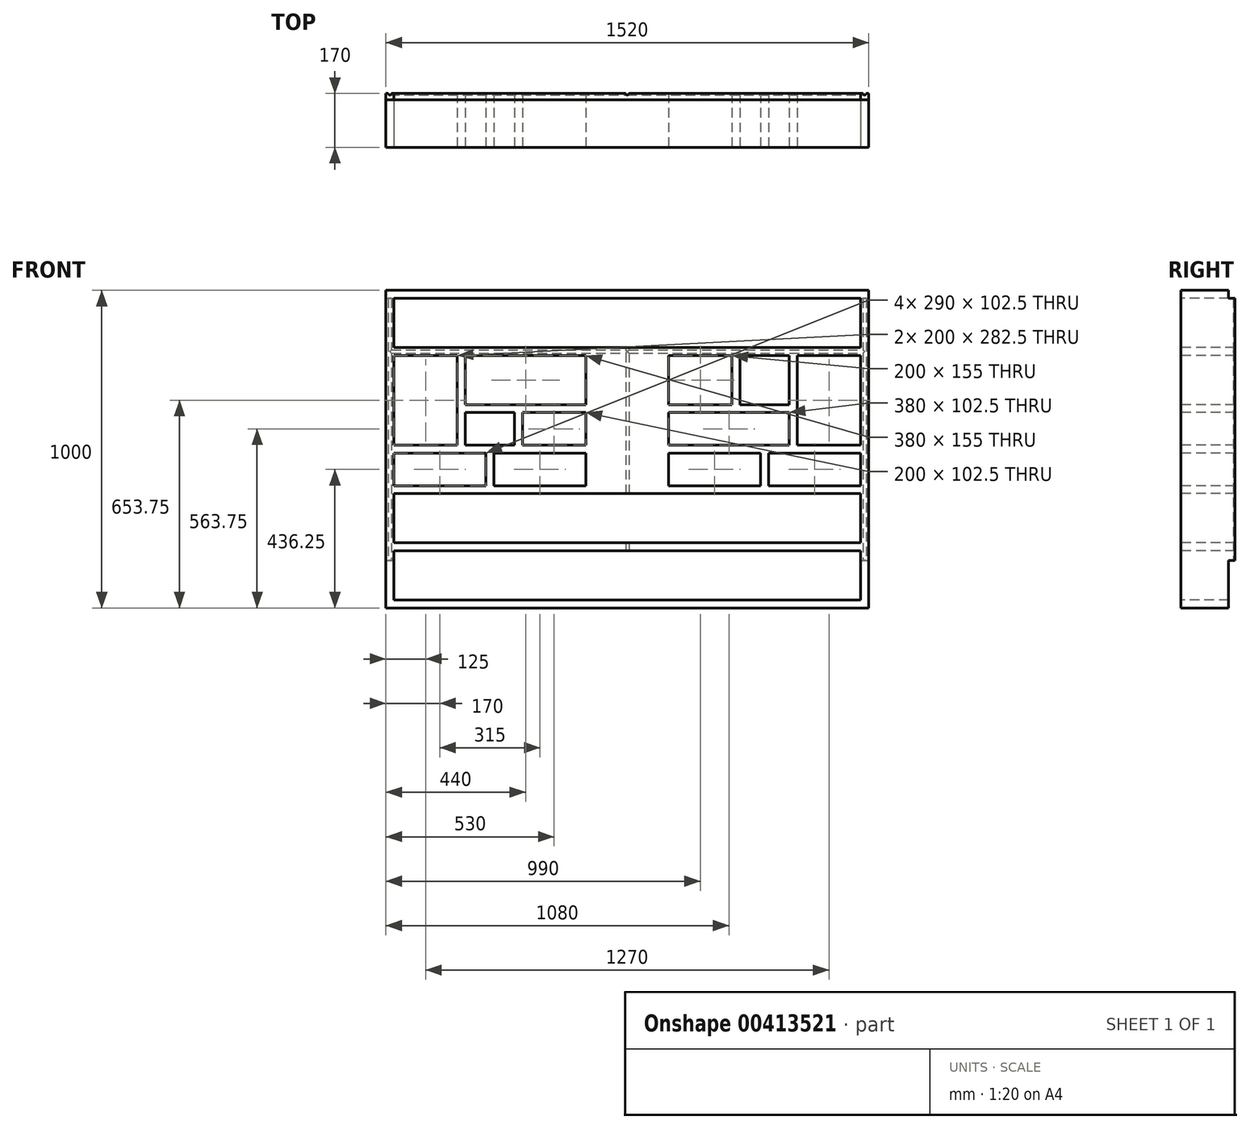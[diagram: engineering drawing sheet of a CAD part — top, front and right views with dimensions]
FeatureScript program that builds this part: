
annotation { "Feature Type Name" : "Feature", "Feature Type Description" : "" }
export const myFeature = defineFeature(function(context is Context, id is Id, definition is map)
    precondition{}
    {
        {
            var Q0;
            Q0=qCreatedBy(makeId("Front.planeOp"),FACE);
            var sketch = newSketch(context, id + "F0", { "sketchPlane" : qUnion([Q0])});
            skLineSegment(sketch, "E0.bottom", {"start": v(760, 500) * mm, "end": v(-760, 500) * mm});
            skLineSegment(sketch, "E0.top", {"start": v(760, -500) * mm, "end": v(-760, -500) * mm});
            skLineSegment(sketch, "E0.left", {"start": v(760, 500) * mm, "end": v(760, -500) * mm});
            skLineSegment(sketch, "E0.right", {"start": v(-760, 500) * mm, "end": v(-760, -500) * mm});
            skPoint(sketch, "E0.middle", {"position": v(0, 0) * mm});
            skSolve(sketch);
        }
        {
            var Q0;
            Q0=makeQuery(id+"F0.imprint","IMPRINT",FACE,{"disambiguationData":[TD([[makeQuery(id+"F0.imprint","IMPRINT",EDGE,{"derivedFrom":sQuery(id+"F0.wireOp",EDGE,"E0.bottom")}),1.0]])]});
            extrude(context, id + "F1", {"entities" : qUnion([Q0]), "oppositeDirection" : true, "offsetDistance" : 25 * mm, "depth" : 170 * mm});
        }
        {
            var Q0;
            Q0=makeQuery(id+"F1.opExtrude","CAP_FACE",FACE,{"disambiguationData":[OSD([sQuery(id+"F0.wireOp",EDGE,"E0.bottom"),sQuery(id+"F0.wireOp",EDGE,"E0.top"),sQuery(id+"F0.wireOp",EDGE,"E0.left"),sQuery(id+"F0.wireOp",EDGE,"E0.right")])],"isStart":true});
            var sketch = newSketch(context, id + "F2", { "sketchPlane" : qUnion([Q0])});
            skLineSegment(sketch, "E1.bottom", {"start": v(-735, -475) * mm, "end": v(735, -475) * mm});
            skLineSegment(sketch, "E1.left", {"start": v(-735, -475) * mm, "end": v(-735, -320) * mm});
            skLineSegment(sketch, "E1.right", {"start": v(735, -475) * mm, "end": v(735, -425) * mm});
            skPoint(sketch, "E2.middle", {"position": v(0, 0) * mm});
            skLineSegment(sketch, "E3", {"start": v(-735, -295) * mm, "end": v(-735, -140) * mm});
            skLineSegment(sketch, "E4", {"start": v(-735, 475) * mm, "end": v(735, 475) * mm});
            skLineSegment(sketch, "E5", {"start": v(735, 475) * mm, "end": v(735, 320) * mm});
            skLineSegment(sketch, "E6", {"start": v(-735, 0) * mm, "end": v(735, 0) * mm, "construction": true});
            skLineSegment(sketch, "E7", {"start": v(-735, -320) * mm, "end": v(735, -320) * mm});
            skLineSegment(sketch, "E8", {"start": v(-735, -295) * mm, "end": v(735, -295) * mm});
            skLineSegment(sketch, "E9", {"start": v(-735, -140) * mm, "end": v(735, -140) * mm});
            skLineSegment(sketch, "E10", {"start": v(-735, -115) * mm, "end": v(735, -115) * mm});
            skLineSegment(sketch, "E11", {"start": v(-735, -12.5) * mm, "end": v(-105, -12.5) * mm});
            skLineSegment(sketch, "E12", {"start": v(-735, 12.5) * mm, "end": v(-105, 12.5) * mm});
            skLineSegment(sketch, "E13.MirrorCS", {"start": v(-735, 320) * mm, "end": v(735, 320) * mm});
            skLineSegment(sketch, "E14.MirrorCS", {"start": v(-735, 295) * mm, "end": v(735, 295) * mm});
            skLineSegment(sketch, "E15.MirrorCS", {"start": v(-535, 115) * mm, "end": v(-105, 115) * mm});
            skLineSegment(sketch, "E16.MirrorCS", {"start": v(-535, 140) * mm, "end": v(-105, 140) * mm});
            skLineSegment(sketch, "E17.trimOffspring", {"start": v(735, 295) * mm, "end": v(735, 140) * mm});
            skLineSegment(sketch, "E18.trimOffspring", {"start": v(-735, 320) * mm, "end": v(-735, 475) * mm});
            skLineSegment(sketch, "E19.trimOffspring", {"start": v(-735, 140) * mm, "end": v(-735, 295) * mm});
            skLineSegment(sketch, "E20.trimOffspring", {"start": v(-735, 12.5) * mm, "end": v(-735, 115) * mm});
            skLineSegment(sketch, "E21.trimOffspring", {"start": v(-735, -115) * mm, "end": v(-735, -12.5) * mm});
            skLineSegment(sketch, "E22.trimOffspring", {"start": v(735, -320) * mm, "end": v(735, -425) * mm});
            skLineSegment(sketch, "E23.trimOffspring", {"start": v(735, -140) * mm, "end": v(735, -295) * mm});
            skLineSegment(sketch, "E24.trimOffspring", {"start": v(735, 115) * mm, "end": v(735, 12.5) * mm});
            skLineSegment(sketch, "E25.trimOffspring", {"start": v(735, -12.5) * mm, "end": v(735, -115) * mm});
            skLineSegment(sketch, "E26", {"start": v(0, 0) * mm, "end": v(0, 295) * mm, "construction": true});
            skLineSegment(sketch, "E27", {"start": v(535, 295) * mm, "end": v(535, 12.5) * mm});
            skLineSegment(sketch, "E28", {"start": v(510, 295) * mm, "end": v(510, 12.5) * mm});
            skLineSegment(sketch, "E29", {"start": v(330, 295) * mm, "end": v(330, 140) * mm});
            skLineSegment(sketch, "E30", {"start": v(355, 295) * mm, "end": v(355, 140) * mm});
            skLineSegment(sketch, "E31.MirrorCS", {"start": v(-510, 295) * mm, "end": v(-510, 12.5) * mm});
            skLineSegment(sketch, "E32.MirrorCS", {"start": v(-535, 295) * mm, "end": v(-535, 12.5) * mm});
            skLineSegment(sketch, "E33", {"start": v(-330, 12.5) * mm, "end": v(-330, 140) * mm});
            skLineSegment(sketch, "E34", {"start": v(-355, 140) * mm, "end": v(-355, 12.5) * mm});
            skPoint(sketch, "E35.MirrorCS.start.orphan", {"position": v(-330, 295) * mm});
            skPoint(sketch, "E36.MirrorCS.start.orphan", {"position": v(-355, 295) * mm});
            skLineSegment(sketch, "E37", {"start": v(-735, 140) * mm, "end": v(-735, 115) * mm});
            skLineSegment(sketch, "E38", {"start": v(735, 115) * mm, "end": v(735, 140) * mm});
            skLineSegment(sketch, "E39", {"start": v(105, 295) * mm, "end": v(105, 12.5) * mm});
            skLineSegment(sketch, "E40", {"start": v(130, 295) * mm, "end": v(130, 12.5) * mm});
            skLineSegment(sketch, "E41.MirrorCS", {"start": v(-130, 295) * mm, "end": v(-130, 12.5) * mm});
            skLineSegment(sketch, "E42.MirrorCS", {"start": v(-105, 295) * mm, "end": v(-105, 12.5) * mm});
            skLineSegment(sketch, "E43.trimOffspring", {"start": v(105, 115) * mm, "end": v(535, 115) * mm});
            skLineSegment(sketch, "E44.trimOffspring", {"start": v(105, 140) * mm, "end": v(535, 140) * mm});
            skLineSegment(sketch, "E45", {"start": v(105, -12.5) * mm, "end": v(105, -115) * mm});
            skLineSegment(sketch, "E46", {"start": v(130, -12.5) * mm, "end": v(130, -115) * mm});
            skLineSegment(sketch, "E47", {"start": v(-130, -12.5) * mm, "end": v(-130, -115) * mm});
            skLineSegment(sketch, "E48", {"start": v(-105, -12.5) * mm, "end": v(-105, -115) * mm});
            skLineSegment(sketch, "E49", {"start": v(-105, 12.5) * mm, "end": v(-105, -12.5) * mm});
            skLineSegment(sketch, "E50", {"start": v(105, 12.5) * mm, "end": v(105, -12.5) * mm});
            skLineSegment(sketch, "E51", {"start": v(130, 12.5) * mm, "end": v(735, 12.5) * mm});
            skLineSegment(sketch, "E52", {"start": v(735, -12.5) * mm, "end": v(130, -12.5) * mm});
            skLineSegment(sketch, "E53", {"start": v(445, -12.5) * mm, "end": v(445, -115) * mm});
            skLineSegment(sketch, "E54", {"start": v(420, -12.5) * mm, "end": v(420, -115) * mm});
            skLineSegment(sketch, "E55", {"start": v(-445, -12.5) * mm, "end": v(-445, -115) * mm});
            skLineSegment(sketch, "E56", {"start": v(-420, -12.5) * mm, "end": v(-420, -115) * mm});
            skSolve(sketch);
        }
        {
            var Q0;
            Q0=makeQuery(id+"F2.imprint","IMPRINT",FACE,{"disambiguationData":[TD([[makeQuery(id+"F2.imprint","IMPRINT",EDGE,{"derivedFrom":sQuery(id+"F2.wireOp",EDGE,"E4")}),-1.0]])]});
            var Q1;
            Q1=makeQuery(id+"F2.imprint","IMPRINT",FACE,{"disambiguationData":[TD([[makeQuery(id+"F2.imprint","IMPRINT",EDGE,{"derivedFrom":sQuery(id+"F2.wireOp",EDGE,"E14.MirrorCS")}),-1.0]])]});
            var Q2;
            Q2=makeQuery(id+"F2.imprint","IMPRINT",FACE,{"disambiguationData":[TD([[makeQuery(id+"F2.imprint","IMPRINT",EDGE,{"derivedFrom":sQuery(id+"F2.wireOp",EDGE,"E12")}),1.0]])]});
            var Q3;
            Q3=makeQuery(id+"F2.imprint","IMPRINT",FACE,{"disambiguationData":[TD([[makeQuery(id+"F2.imprint","IMPRINT",EDGE,{"derivedFrom":sQuery(id+"F2.wireOp",EDGE,"E10")}),1.0]])]});
            var Q4;
            Q4=makeQuery(id+"F2.imprint","IMPRINT",FACE,{"disambiguationData":[TD([[makeQuery(id+"F2.imprint","IMPRINT",EDGE,{"derivedFrom":sQuery(id+"F2.wireOp",EDGE,"E3")}),-1.0]])]});
            var Q5;
            Q5=makeQuery(id+"F2.imprint","IMPRINT",FACE,{"disambiguationData":[TD([[makeQuery(id+"F2.imprint","IMPRINT",EDGE,{"derivedFrom":sQuery(id+"F2.wireOp",EDGE,"E1.bottom")}),1.0]])]});
            var Q6;
            Q6=makeQuery(id+"F1.opExtrude","CAP_FACE",FACE,{"disambiguationData":[OSD([sQuery(id+"F0.wireOp",EDGE,"E0.bottom"),sQuery(id+"F0.wireOp",EDGE,"E0.top"),sQuery(id+"F0.wireOp",EDGE,"E0.left"),sQuery(id+"F0.wireOp",EDGE,"E0.right")])],"isStart":false});
            extrude(context, id + "F3", {"entities" : qUnion([Q0, Q1, Q2, Q3, Q4, Q5]), "operationType" : NewBodyOperationType.REMOVE, "endBound" : BoundingType.UP_TO_SURFACE, "oppositeDirection" : true, "depth" : 25 * mm, "endBoundEntityFace" : qUnion([Q6]), "offsetDistance" : 25 * mm});
        }
        {
            var Q0;
            {var subQ0=sQuery(id+"F2.wireOp",EDGE,"E31.MirrorCS");var subQ1=sQuery(id+"F2.wireOp",EDGE,"E14.MirrorCS");var subQ2=makeQuery(id+"F2.imprint","INTERSECT",VERTEX,{"derivedFrom":[subQ1,subQ0]});Q0=makeQuery(id+"F2.imprint","IMPRINT",FACE,{"disambiguationData":[TD([[makeQuery(id+"F2.imprint","IMPRINT",EDGE,{"disambiguationData":[TD([[subQ2,1.0]])],"derivedFrom":subQ1}),-1.0]])]});}
            var Q1;
            {var subQ0=sQuery(id+"F2.wireOp",EDGE,"E32.MirrorCS");var subQ1=sQuery(id+"F2.wireOp",EDGE,"E15.MirrorCS");var subQ2=makeQuery(id+"F2.imprint","INTERSECT",VERTEX,{"derivedFrom":[subQ1,subQ0]});Q1=makeQuery(id+"F2.imprint","IMPRINT",FACE,{"disambiguationData":[TD([[makeQuery(id+"F2.imprint","IMPRINT",EDGE,{"disambiguationData":[TD([[subQ2,-1.0]])],"derivedFrom":subQ1}),1.0]])]});}
            var Q2;
            {var subQ0=sQuery(id+"F2.wireOp",EDGE,"E31.MirrorCS");var subQ1=sQuery(id+"F2.wireOp",EDGE,"E12");var subQ2=makeQuery(id+"F2.imprint","INTERSECT",VERTEX,{"derivedFrom":[subQ1,subQ0]});Q2=makeQuery(id+"F2.imprint","IMPRINT",FACE,{"disambiguationData":[TD([[makeQuery(id+"F2.imprint","IMPRINT",EDGE,{"disambiguationData":[TD([[subQ2,1.0]])],"derivedFrom":subQ1}),1.0]])]});}
            var Q3;
            {var subQ0=sQuery(id+"F2.wireOp",EDGE,"E31.MirrorCS");var subQ1=sQuery(id+"F2.wireOp",EDGE,"E15.MirrorCS");var subQ2=makeQuery(id+"F2.imprint","INTERSECT",VERTEX,{"derivedFrom":[subQ1,subQ0]});Q3=makeQuery(id+"F2.imprint","IMPRINT",FACE,{"disambiguationData":[TD([[makeQuery(id+"F2.imprint","IMPRINT",EDGE,{"disambiguationData":[TD([[subQ2,-1.0]])],"derivedFrom":subQ1}),1.0]])]});}
            var Q4;
            {var subQ0=sQuery(id+"F2.wireOp",EDGE,"E34");var subQ1=sQuery(id+"F2.wireOp",EDGE,"E15.MirrorCS");var subQ2=makeQuery(id+"F2.imprint","INTERSECT",VERTEX,{"derivedFrom":[subQ1,subQ0]});Q4=makeQuery(id+"F2.imprint","IMPRINT",FACE,{"disambiguationData":[TD([[makeQuery(id+"F2.imprint","IMPRINT",EDGE,{"disambiguationData":[TD([[subQ2,-1.0]])],"derivedFrom":subQ1}),1.0]])]});}
            var Q5;
            {var subQ0=sQuery(id+"F2.wireOp",EDGE,"E33");var subQ1=sQuery(id+"F2.wireOp",EDGE,"E12");var subQ2=makeQuery(id+"F2.imprint","INTERSECT",VERTEX,{"derivedFrom":[subQ1,subQ0]});Q5=makeQuery(id+"F2.imprint","IMPRINT",FACE,{"disambiguationData":[TD([[makeQuery(id+"F2.imprint","IMPRINT",EDGE,{"disambiguationData":[TD([[subQ2,1.0]])],"derivedFrom":subQ1}),1.0]])]});}
            var Q6;
            {var subQ0=sQuery(id+"F2.wireOp",EDGE,"E33");var subQ1=sQuery(id+"F2.wireOp",EDGE,"E15.MirrorCS");var subQ2=makeQuery(id+"F2.imprint","INTERSECT",VERTEX,{"derivedFrom":[subQ1,subQ0]});Q6=makeQuery(id+"F2.imprint","IMPRINT",FACE,{"disambiguationData":[TD([[makeQuery(id+"F2.imprint","IMPRINT",EDGE,{"disambiguationData":[TD([[subQ2,-1.0]])],"derivedFrom":subQ1}),1.0]])]});}
            var Q7;
            {var subQ0=sQuery(id+"F2.wireOp",EDGE,"eI3SPyVD-0uEl-pIWH-4MRa-sc1sVIOGqZNf");var subQ1=sQuery(id+"F2.wireOp",EDGE,"E12");var subQ2=makeQuery(id+"F2.imprint","INTERSECT",VERTEX,{"derivedFrom":[subQ1,subQ0]});Q7=makeQuery(id+"F2.imprint","IMPRINT",FACE,{"disambiguationData":[TD([[makeQuery(id+"F2.imprint","IMPRINT",EDGE,{"disambiguationData":[TD([[subQ2,1.0]])],"derivedFrom":subQ1}),1.0]])]});}
            var Q8;
            {var subQ0=sQuery(id+"F2.wireOp",EDGE,"ZKDIpnAd-JpXH-PnlA-Ugrf-fCPR0U1nQhHu");var subQ1=sQuery(id+"F2.wireOp",EDGE,"E15.MirrorCS");var subQ2=makeQuery(id+"F2.imprint","INTERSECT",VERTEX,{"derivedFrom":[subQ1,subQ0]});Q8=makeQuery(id+"F2.imprint","IMPRINT",FACE,{"disambiguationData":[TD([[makeQuery(id+"F2.imprint","IMPRINT",EDGE,{"disambiguationData":[TD([[subQ2,-1.0]])],"derivedFrom":subQ1}),1.0]])]});}
            var Q9;
            {var subQ0=sQuery(id+"F2.wireOp",EDGE,"eI3SPyVD-0uEl-pIWH-4MRa-sc1sVIOGqZNf");var subQ1=sQuery(id+"F2.wireOp",EDGE,"E14.MirrorCS");var subQ2=makeQuery(id+"F2.imprint","INTERSECT",VERTEX,{"derivedFrom":[subQ1,subQ0]});Q9=makeQuery(id+"F2.imprint","IMPRINT",FACE,{"disambiguationData":[TD([[makeQuery(id+"F2.imprint","IMPRINT",EDGE,{"disambiguationData":[TD([[subQ2,1.0]])],"derivedFrom":subQ1}),-1.0]])]});}
            var Q10;
            {var subQ0=sQuery(id+"F2.wireOp",EDGE,"E29");Q10=makeQuery(id+"F2.imprint","IMPRINT",FACE,{"disambiguationData":[TD([[makeQuery(id+"F2.imprint","IMPRINT",EDGE,{"derivedFrom":subQ0}),1.0]])]});}
            var Q11;
            {var subQ5=sQuery(id+"F2.wireOp",EDGE,"eI3SPyVD-0uEl-pIWH-4MRa-sc1sVIOGqZNf");var subQ6=sQuery(id+"F2.wireOp",EDGE,"E15.MirrorCS");var subQ7=makeQuery(id+"F2.imprint","INTERSECT",VERTEX,{"derivedFrom":[subQ6,subQ5]});Q11=makeQuery(id+"F2.imprint","IMPRINT",FACE,{"disambiguationData":[TD([[makeQuery(id+"F2.imprint","IMPRINT",EDGE,{"disambiguationData":[TD([[subQ7,-1.0]])],"derivedFrom":subQ6}),1.0]])]});}
            var Q12;
            {var subQ0=sQuery(id+"F2.wireOp",EDGE,"E27");var subQ1=sQuery(id+"F2.wireOp",EDGE,"E12");var subQ2=makeQuery(id+"F2.imprint","INTERSECT",VERTEX,{"derivedFrom":[subQ1,subQ0]});Q12=makeQuery(id+"F2.imprint","IMPRINT",FACE,{"disambiguationData":[TD([[makeQuery(id+"F2.imprint","IMPRINT",EDGE,{"disambiguationData":[TD([[subQ2,1.0]])],"derivedFrom":subQ1}),1.0]])]});}
            var Q13;
            {var subQ0=sQuery(id+"F2.wireOp",EDGE,"E27");var subQ1=sQuery(id+"F2.wireOp",EDGE,"E15.MirrorCS");var subQ2=makeQuery(id+"F2.imprint","INTERSECT",VERTEX,{"derivedFrom":[subQ1,subQ0]});Q13=makeQuery(id+"F2.imprint","IMPRINT",FACE,{"disambiguationData":[TD([[makeQuery(id+"F2.imprint","IMPRINT",EDGE,{"disambiguationData":[TD([[subQ2,1.0]])],"derivedFrom":subQ1}),1.0]])]});}
            var Q14;
            {var subQ0=sQuery(id+"F2.wireOp",EDGE,"E27");var subQ1=sQuery(id+"F2.wireOp",EDGE,"E14.MirrorCS");var subQ2=makeQuery(id+"F2.imprint","INTERSECT",VERTEX,{"derivedFrom":[subQ1,subQ0]});Q14=makeQuery(id+"F2.imprint","IMPRINT",FACE,{"disambiguationData":[TD([[makeQuery(id+"F2.imprint","IMPRINT",EDGE,{"disambiguationData":[TD([[subQ2,1.0]])],"derivedFrom":subQ1}),-1.0]])]});}
            var Q15;
            Q15=makeQuery(id+"F1.opExtrude","CAP_FACE",FACE,{"disambiguationData":[OSD([sQuery(id+"F0.wireOp",EDGE,"E0.bottom"),sQuery(id+"F0.wireOp",EDGE,"E0.top"),sQuery(id+"F0.wireOp",EDGE,"E0.left"),sQuery(id+"F0.wireOp",EDGE,"E0.right")])],"isStart":false});
            extrude(context, id + "F4", {"entities" : qUnion([Q0, Q1, Q2, Q3, Q4, Q5, Q6, Q7, Q8, Q9, Q10, Q11, Q12, Q13, Q14]), "operationType" : NewBodyOperationType.ADD, "endBound" : BoundingType.UP_TO_SURFACE, "oppositeDirection" : true, "depth" : 25 * mm, "endBoundEntityFace" : qUnion([Q15]), "offsetDistance" : 25 * mm});
        }
        {
            var Q0;
            {var subQ1=sQuery(id+"F2.wireOp",EDGE,"E19.trimOffspring");Q0=makeQuery(id+"F2.imprint","IMPRINT",FACE,{"disambiguationData":[TD([[makeQuery(id+"F2.imprint","IMPRINT",EDGE,{"derivedFrom":subQ1}),-1.0]])]});}
            var Q1;
            {var subQ2=sQuery(id+"F2.wireOp",EDGE,"ZKDIpnAd-JpXH-PnlA-Ugrf-fCPR0U1nQhHu");var subQ7=sQuery(id+"F2.wireOp",EDGE,"E14.MirrorCS");var subQ8=makeQuery(id+"F2.imprint","INTERSECT",VERTEX,{"derivedFrom":[subQ7,subQ2]});Q1=makeQuery(id+"F2.imprint","IMPRINT",FACE,{"disambiguationData":[TD([[makeQuery(id+"F2.imprint","IMPRINT",EDGE,{"disambiguationData":[TD([[subQ8,1.0]])],"derivedFrom":subQ7}),-1.0]])]});}
            var Q2;
            {var subQ1=sQuery(id+"F2.wireOp",EDGE,"E17.trimOffspring");Q2=makeQuery(id+"F2.imprint","IMPRINT",FACE,{"disambiguationData":[TD([[makeQuery(id+"F2.imprint","IMPRINT",EDGE,{"derivedFrom":subQ1}),-1.0]])]});}
            var Q3;
            Q3=makeQuery(id+"F4.boolean.opBoolean","MERGE",FACE,{"derivedFrom":[makeQuery(id+"F1.opExtrude","CAP_FACE",FACE,{"disambiguationData":[OSD([sQuery(id+"F0.wireOp",EDGE,"E0.bottom"),sQuery(id+"F0.wireOp",EDGE,"E0.top"),sQuery(id+"F0.wireOp",EDGE,"E0.left"),sQuery(id+"F0.wireOp",EDGE,"E0.right")])],"isStart":false}),makeQuery(id+"F4.opExtrude","CAP_FACE",FACE,{"disambiguationData":[OSD([sQuery(id+"F2.wireOp",EDGE,"E12"),sQuery(id+"F2.wireOp",EDGE,"E14.MirrorCS"),sQuery(id+"F2.wireOp",EDGE,"E15.MirrorCS"),sQuery(id+"F2.wireOp",EDGE,"E16.MirrorCS"),sQuery(id+"F2.wireOp",EDGE,"eI3SPyVD-0uEl-pIWH-4MRa-sc1sVIOGqZNf"),sQuery(id+"F2.wireOp",EDGE,"ZKDIpnAd-JpXH-PnlA-Ugrf-fCPR0U1nQhHu"),sQuery(id+"F2.wireOp",EDGE,"E27"),sQuery(id+"F2.wireOp",EDGE,"E28"),sQuery(id+"F2.wireOp",EDGE,"E29"),sQuery(id+"F2.wireOp",EDGE,"E30"),sQuery(id+"F2.wireOp",EDGE,"E31.MirrorCS"),sQuery(id+"F2.wireOp",EDGE,"E32.MirrorCS"),sQuery(id+"F2.wireOp",EDGE,"E33"),sQuery(id+"F2.wireOp",EDGE,"E34")])],"isStart":false})]});
            extrude(context, id + "F5", {"entities" : qUnion([Q0, Q1, Q2]), "operationType" : NewBodyOperationType.REMOVE, "endBound" : BoundingType.UP_TO_SURFACE, "oppositeDirection" : true, "depth" : 25 * mm, "endBoundEntityFace" : qUnion([Q3]), "offsetDistance" : 25 * mm});
        }
        {
            var Q0;
            {var subQ0=sQuery(id+"F2.wireOp",EDGE,"E29");Q0=makeQuery(id+"F2.imprint","IMPRINT",FACE,{"disambiguationData":[TD([[makeQuery(id+"F2.imprint","IMPRINT",EDGE,{"derivedFrom":subQ0}),1.0]])]});}
            var Q1;
            {var subQ0=sQuery(id+"F2.wireOp",EDGE,"E44.trimOffspring");var subQ5=sQuery(id+"F2.wireOp",EDGE,"E28");var subQ8=makeQuery(id+"F2.imprint","INTERSECT",VERTEX,{"derivedFrom":[subQ5,subQ0]});Q1=makeQuery(id+"F2.imprint","IMPRINT",FACE,{"disambiguationData":[TD([[makeQuery(id+"F2.imprint","IMPRINT",EDGE,{"disambiguationData":[TD([[subQ8,-1.0]])],"derivedFrom":subQ5}),-1.0]])]});}
            var Q2;
            {var subQ0=sQuery(id+"F2.wireOp",EDGE,"E27");var subQ1=sQuery(id+"F2.wireOp",EDGE,"E14.MirrorCS");var subQ2=makeQuery(id+"F2.imprint","INTERSECT",VERTEX,{"derivedFrom":[subQ1,subQ0]});Q2=makeQuery(id+"F2.imprint","IMPRINT",FACE,{"disambiguationData":[TD([[makeQuery(id+"F2.imprint","IMPRINT",EDGE,{"disambiguationData":[TD([[subQ2,1.0]])],"derivedFrom":subQ1}),-1.0]])]});}
            var Q3;
            {var subQ0=sQuery(id+"F2.wireOp",EDGE,"E43.trimOffspring");var subQ1=sQuery(id+"F2.wireOp",EDGE,"E27");var subQ2=makeQuery(id+"F2.imprint","INTERSECT",VERTEX,{"derivedFrom":[subQ1,subQ0]});Q3=makeQuery(id+"F2.imprint","IMPRINT",FACE,{"disambiguationData":[TD([[makeQuery(id+"F2.imprint","IMPRINT",EDGE,{"disambiguationData":[TD([[subQ2,1.0]])],"derivedFrom":subQ1}),-1.0]])]});}
            var Q4;
            {var subQ0=sQuery(id+"F2.wireOp",EDGE,"E27");var subQ1=sQuery(id+"F2.wireOp",EDGE,"E12");var subQ2=makeQuery(id+"F2.imprint","INTERSECT",VERTEX,{"derivedFrom":[subQ1,subQ0]});Q4=makeQuery(id+"F2.imprint","IMPRINT",FACE,{"disambiguationData":[TD([[makeQuery(id+"F2.imprint","IMPRINT",EDGE,{"disambiguationData":[TD([[subQ2,1.0]])],"derivedFrom":subQ1}),1.0]])]});}
            var Q5;
            {var subQ0=sQuery(id+"F2.wireOp",EDGE,"E39");var subQ1=sQuery(id+"F2.wireOp",EDGE,"E12");var subQ2=makeQuery(id+"F2.imprint","INTERSECT",VERTEX,{"derivedFrom":[subQ1,subQ0]});Q5=makeQuery(id+"F2.imprint","IMPRINT",FACE,{"disambiguationData":[TD([[makeQuery(id+"F2.imprint","IMPRINT",EDGE,{"disambiguationData":[TD([[subQ2,-1.0]])],"derivedFrom":subQ1}),1.0]])]});}
            var Q6;
            {var subQ0=sQuery(id+"F2.wireOp",EDGE,"E43.trimOffspring");var subQ1=sQuery(id+"F2.wireOp",EDGE,"E39");var subQ2=makeQuery(id+"F2.imprint","INTERSECT",VERTEX,{"derivedFrom":[subQ1,subQ0]});Q6=makeQuery(id+"F2.imprint","IMPRINT",FACE,{"disambiguationData":[TD([[makeQuery(id+"F2.imprint","IMPRINT",EDGE,{"disambiguationData":[TD([[subQ2,1.0]])],"derivedFrom":subQ1}),1.0]])]});}
            var Q7;
            {var subQ0=sQuery(id+"F2.wireOp",EDGE,"E39");var subQ1=sQuery(id+"F2.wireOp",EDGE,"E14.MirrorCS");var subQ2=makeQuery(id+"F2.imprint","INTERSECT",VERTEX,{"derivedFrom":[subQ1,subQ0]});Q7=makeQuery(id+"F2.imprint","IMPRINT",FACE,{"disambiguationData":[TD([[makeQuery(id+"F2.imprint","IMPRINT",EDGE,{"disambiguationData":[TD([[subQ2,-1.0]])],"derivedFrom":subQ1}),-1.0]])]});}
            var Q8;
            {var subQ0=sQuery(id+"F2.wireOp",EDGE,"E41.MirrorCS");var subQ1=sQuery(id+"F2.wireOp",EDGE,"E14.MirrorCS");var subQ2=makeQuery(id+"F2.imprint","INTERSECT",VERTEX,{"derivedFrom":[subQ1,subQ0]});Q8=makeQuery(id+"F2.imprint","IMPRINT",FACE,{"disambiguationData":[TD([[makeQuery(id+"F2.imprint","IMPRINT",EDGE,{"disambiguationData":[TD([[subQ2,-1.0]])],"derivedFrom":subQ1}),-1.0]])]});}
            var Q9;
            {var subQ0=sQuery(id+"F2.wireOp",EDGE,"E42.MirrorCS");var subQ1=sQuery(id+"F2.wireOp",EDGE,"E15.MirrorCS");var subQ2=makeQuery(id+"F2.imprint","INTERSECT",VERTEX,{"derivedFrom":[subQ1,subQ0]});Q9=makeQuery(id+"F2.imprint","IMPRINT",FACE,{"disambiguationData":[TD([[makeQuery(id+"F2.imprint","IMPRINT",EDGE,{"disambiguationData":[TD([[subQ2,1.0]])],"derivedFrom":subQ1}),1.0]])]});}
            var Q10;
            {var subQ0=sQuery(id+"F2.wireOp",EDGE,"E41.MirrorCS");var subQ1=sQuery(id+"F2.wireOp",EDGE,"E12");var subQ2=makeQuery(id+"F2.imprint","INTERSECT",VERTEX,{"derivedFrom":[subQ1,subQ0]});Q10=makeQuery(id+"F2.imprint","IMPRINT",FACE,{"disambiguationData":[TD([[makeQuery(id+"F2.imprint","IMPRINT",EDGE,{"disambiguationData":[TD([[subQ2,-1.0]])],"derivedFrom":subQ1}),1.0]])]});}
            var Q11;
            {var subQ0=sQuery(id+"F2.wireOp",EDGE,"E33");var subQ1=sQuery(id+"F2.wireOp",EDGE,"E15.MirrorCS");var subQ2=makeQuery(id+"F2.imprint","INTERSECT",VERTEX,{"derivedFrom":[subQ1,subQ0]});Q11=makeQuery(id+"F2.imprint","IMPRINT",FACE,{"disambiguationData":[TD([[makeQuery(id+"F2.imprint","IMPRINT",EDGE,{"disambiguationData":[TD([[subQ2,-1.0]])],"derivedFrom":subQ1}),1.0]])]});}
            var Q12;
            {var subQ0=sQuery(id+"F2.wireOp",EDGE,"E33");var subQ1=sQuery(id+"F2.wireOp",EDGE,"E12");var subQ2=makeQuery(id+"F2.imprint","INTERSECT",VERTEX,{"derivedFrom":[subQ1,subQ0]});Q12=makeQuery(id+"F2.imprint","IMPRINT",FACE,{"disambiguationData":[TD([[makeQuery(id+"F2.imprint","IMPRINT",EDGE,{"disambiguationData":[TD([[subQ2,1.0]])],"derivedFrom":subQ1}),1.0]])]});}
            var Q13;
            {var subQ0=sQuery(id+"F2.wireOp",EDGE,"E34");var subQ1=sQuery(id+"F2.wireOp",EDGE,"E15.MirrorCS");var subQ2=makeQuery(id+"F2.imprint","INTERSECT",VERTEX,{"derivedFrom":[subQ1,subQ0]});Q13=makeQuery(id+"F2.imprint","IMPRINT",FACE,{"disambiguationData":[TD([[makeQuery(id+"F2.imprint","IMPRINT",EDGE,{"disambiguationData":[TD([[subQ2,-1.0]])],"derivedFrom":subQ1}),1.0]])]});}
            var Q14;
            {var subQ0=sQuery(id+"F2.wireOp",EDGE,"E31.MirrorCS");var subQ1=sQuery(id+"F2.wireOp",EDGE,"E15.MirrorCS");var subQ2=makeQuery(id+"F2.imprint","INTERSECT",VERTEX,{"derivedFrom":[subQ1,subQ0]});Q14=makeQuery(id+"F2.imprint","IMPRINT",FACE,{"disambiguationData":[TD([[makeQuery(id+"F2.imprint","IMPRINT",EDGE,{"disambiguationData":[TD([[subQ2,-1.0]])],"derivedFrom":subQ1}),1.0]])]});}
            var Q15;
            {var subQ0=sQuery(id+"F2.wireOp",EDGE,"E31.MirrorCS");var subQ1=sQuery(id+"F2.wireOp",EDGE,"E12");var subQ2=makeQuery(id+"F2.imprint","INTERSECT",VERTEX,{"derivedFrom":[subQ1,subQ0]});Q15=makeQuery(id+"F2.imprint","IMPRINT",FACE,{"disambiguationData":[TD([[makeQuery(id+"F2.imprint","IMPRINT",EDGE,{"disambiguationData":[TD([[subQ2,1.0]])],"derivedFrom":subQ1}),1.0]])]});}
            var Q16;
            {var subQ0=sQuery(id+"F2.wireOp",EDGE,"E32.MirrorCS");var subQ1=sQuery(id+"F2.wireOp",EDGE,"E15.MirrorCS");var subQ2=makeQuery(id+"F2.imprint","INTERSECT",VERTEX,{"derivedFrom":[subQ1,subQ0]});Q16=makeQuery(id+"F2.imprint","IMPRINT",FACE,{"disambiguationData":[TD([[makeQuery(id+"F2.imprint","IMPRINT",EDGE,{"disambiguationData":[TD([[subQ2,-1.0]])],"derivedFrom":subQ1}),1.0]])]});}
            var Q17;
            {var subQ0=sQuery(id+"F2.wireOp",EDGE,"E31.MirrorCS");var subQ1=sQuery(id+"F2.wireOp",EDGE,"E14.MirrorCS");var subQ2=makeQuery(id+"F2.imprint","INTERSECT",VERTEX,{"derivedFrom":[subQ1,subQ0]});Q17=makeQuery(id+"F2.imprint","IMPRINT",FACE,{"disambiguationData":[TD([[makeQuery(id+"F2.imprint","IMPRINT",EDGE,{"disambiguationData":[TD([[subQ2,1.0]])],"derivedFrom":subQ1}),-1.0]])]});}
            var Q18;
            {var subQ0=sQuery(id+"F2.wireOp",EDGE,"E39");var subQ1=sQuery(id+"F2.wireOp",EDGE,"E27");var subQ2=sQuery(id+"F2.wireOp",EDGE,"E14.MirrorCS");var subQ3=sQuery(id+"F2.wireOp",EDGE,"E12");Q18=makeQuery(id+"F4.boolean.opBoolean","MERGE",FACE,{"derivedFrom":[makeQuery(id+"F1.opExtrude","CAP_FACE",FACE,{"disambiguationData":[OSD([sQuery(id+"F0.wireOp",EDGE,"E0.bottom"),sQuery(id+"F0.wireOp",EDGE,"E0.top"),sQuery(id+"F0.wireOp",EDGE,"E0.left"),sQuery(id+"F0.wireOp",EDGE,"E0.right")])],"isStart":false}),makeQuery(id+"F4.opExtrude","CAP_FACE",FACE,{"disambiguationData":[OSD([subQ3,subQ2,sQuery(id+"F2.wireOp",EDGE,"E16.MirrorCS"),sQuery(id+"F2.wireOp",EDGE,"E31.MirrorCS"),sQuery(id+"F2.wireOp",EDGE,"E32.MirrorCS"),sQuery(id+"F2.wireOp",EDGE,"E41.MirrorCS"),sQuery(id+"F2.wireOp",EDGE,"E42.MirrorCS")])],"isStart":false}),makeQuery(id+"F4.opExtrude","CAP_FACE",FACE,{"disambiguationData":[OSD([subQ3,subQ1,subQ0,sQuery(id+"F2.wireOp",EDGE,"E43.trimOffspring")])],"isStart":false}),makeQuery(id+"F4.opExtrude","CAP_FACE",FACE,{"disambiguationData":[OSD([subQ2,subQ1,subQ0,sQuery(id+"F2.wireOp",EDGE,"E44.trimOffspring")])],"isStart":false})]});}
            extrude(context, id + "F6", {"entities" : qUnion([Q0, Q1, Q2, Q3, Q4, Q5, Q6, Q7, Q8, Q9, Q10, Q11, Q12, Q13, Q14, Q15, Q16, Q17]), "operationType" : NewBodyOperationType.ADD, "endBound" : BoundingType.UP_TO_SURFACE, "oppositeDirection" : true, "depth" : 25 * mm, "endBoundEntityFace" : qUnion([Q18]), "offsetDistance" : 25 * mm});
        }
        {
            var Q0;
            {var subQ5=sQuery(id+"F2.wireOp",EDGE,"E31.MirrorCS");var subQ7=sQuery(id+"F2.wireOp",EDGE,"E14.MirrorCS");var subQ8=makeQuery(id+"F2.imprint","INTERSECT",VERTEX,{"derivedFrom":[subQ7,subQ5]});Q0=makeQuery(id+"F2.imprint","IMPRINT",FACE,{"disambiguationData":[TD([[makeQuery(id+"F2.imprint","IMPRINT",EDGE,{"disambiguationData":[TD([[subQ8,-1.0]])],"derivedFrom":subQ7}),-1.0]])]});}
            var Q1;
            {var subQ0=sQuery(id+"F2.wireOp",EDGE,"E33");var subQ1=sQuery(id+"F2.wireOp",EDGE,"E12");var subQ2=makeQuery(id+"F2.imprint","INTERSECT",VERTEX,{"derivedFrom":[subQ1,subQ0]});Q1=makeQuery(id+"F2.imprint","IMPRINT",FACE,{"disambiguationData":[TD([[makeQuery(id+"F2.imprint","IMPRINT",EDGE,{"disambiguationData":[TD([[subQ2,-1.0]])],"derivedFrom":subQ1}),1.0]])]});}
            var Q2;
            {var subQ0=sQuery(id+"F2.wireOp",EDGE,"E31.MirrorCS");var subQ1=sQuery(id+"F2.wireOp",EDGE,"E12");var subQ2=makeQuery(id+"F2.imprint","INTERSECT",VERTEX,{"derivedFrom":[subQ1,subQ0]});Q2=makeQuery(id+"F2.imprint","IMPRINT",FACE,{"disambiguationData":[TD([[makeQuery(id+"F2.imprint","IMPRINT",EDGE,{"disambiguationData":[TD([[subQ2,-1.0]])],"derivedFrom":subQ1}),1.0]])]});}
            var Q3;
            {var subQ0=sQuery(id+"F2.wireOp",EDGE,"E39");var subQ7=sQuery(id+"F2.wireOp",EDGE,"E12");var subQ11=makeQuery(id+"F2.imprint","INTERSECT",VERTEX,{"derivedFrom":[subQ7,subQ0]});Q3=makeQuery(id+"F2.imprint","IMPRINT",FACE,{"disambiguationData":[TD([[makeQuery(id+"F2.imprint","IMPRINT",EDGE,{"disambiguationData":[TD([[subQ11,1.0]])],"derivedFrom":subQ7}),1.0]])]});}
            var Q4;
            {var subQ0=sQuery(id+"F2.wireOp",EDGE,"E29");Q4=makeQuery(id+"F2.imprint","IMPRINT",FACE,{"disambiguationData":[TD([[makeQuery(id+"F2.imprint","IMPRINT",EDGE,{"derivedFrom":subQ0}),-1.0]])]});}
            var Q5;
            {var subQ3=sQuery(id+"F2.wireOp",EDGE,"E30");Q5=makeQuery(id+"F2.imprint","IMPRINT",FACE,{"disambiguationData":[TD([[makeQuery(id+"F2.imprint","IMPRINT",EDGE,{"derivedFrom":subQ3}),1.0]])]});}
            var Q6;
            {var subQ0=sQuery(id+"F2.wireOp",EDGE,"E28");var subQ1=sQuery(id+"F2.wireOp",EDGE,"E12");var subQ2=makeQuery(id+"F2.imprint","INTERSECT",VERTEX,{"derivedFrom":[subQ1,subQ0]});Q6=makeQuery(id+"F2.imprint","IMPRINT",FACE,{"disambiguationData":[TD([[makeQuery(id+"F2.imprint","IMPRINT",EDGE,{"disambiguationData":[TD([[subQ2,1.0]])],"derivedFrom":subQ1}),1.0]])]});}
            var Q7;
            {var subQ0=sQuery(id+"F2.wireOp",EDGE,"E44.trimOffspring");var subQ1=sQuery(id+"F2.wireOp",EDGE,"E43.trimOffspring");var subQ2=sQuery(id+"F2.wireOp",EDGE,"E39");var subQ3=sQuery(id+"F2.wireOp",EDGE,"E27");var subQ4=sQuery(id+"F2.wireOp",EDGE,"E14.MirrorCS");var subQ5=sQuery(id+"F2.wireOp",EDGE,"E12");var subQ6=sQuery(id+"F2.wireOp",EDGE,"E42.MirrorCS");var subQ7=sQuery(id+"F2.wireOp",EDGE,"E41.MirrorCS");var subQ8=sQuery(id+"F2.wireOp",EDGE,"E32.MirrorCS");var subQ9=sQuery(id+"F2.wireOp",EDGE,"E31.MirrorCS");var subQ10=sQuery(id+"F2.wireOp",EDGE,"E16.MirrorCS");Q7=makeQuery(id+"F6.boolean.opBoolean","MERGE",FACE,{"derivedFrom":[makeQuery(id+"F4.boolean.opBoolean","MERGE",FACE,{"derivedFrom":[makeQuery(id+"F1.opExtrude","CAP_FACE",FACE,{"disambiguationData":[OSD([sQuery(id+"F0.wireOp",EDGE,"E0.bottom"),sQuery(id+"F0.wireOp",EDGE,"E0.top"),sQuery(id+"F0.wireOp",EDGE,"E0.left"),sQuery(id+"F0.wireOp",EDGE,"E0.right")])],"isStart":false}),makeQuery(id+"F4.opExtrude","CAP_FACE",FACE,{"disambiguationData":[OSD([subQ5,subQ4,subQ10,subQ9,subQ8,subQ7,subQ6])],"isStart":false}),makeQuery(id+"F4.opExtrude","CAP_FACE",FACE,{"disambiguationData":[OSD([subQ5,subQ3,subQ2,subQ1])],"isStart":false}),makeQuery(id+"F4.opExtrude","CAP_FACE",FACE,{"disambiguationData":[OSD([subQ4,subQ3,subQ2,subQ0])],"isStart":false})]}),makeQuery(id+"F6.opExtrude","CAP_FACE",FACE,{"disambiguationData":[OSD([subQ5,subQ4,sQuery(id+"F2.wireOp",EDGE,"E15.MirrorCS"),subQ10,subQ9,subQ8,sQuery(id+"F2.wireOp",EDGE,"E33"),sQuery(id+"F2.wireOp",EDGE,"E34"),subQ7,subQ6])],"isStart":false}),makeQuery(id+"F6.opExtrude","CAP_FACE",FACE,{"disambiguationData":[OSD([subQ5,subQ4,subQ3,sQuery(id+"F2.wireOp",EDGE,"E28"),sQuery(id+"F2.wireOp",EDGE,"E29"),sQuery(id+"F2.wireOp",EDGE,"E30"),subQ2,sQuery(id+"F2.wireOp",EDGE,"E40"),subQ1,subQ0])],"isStart":false})]});}
            extrude(context, id + "F7", {"entities" : qUnion([Q0, Q1, Q2, Q3, Q4, Q5, Q6]), "operationType" : NewBodyOperationType.REMOVE, "endBound" : BoundingType.UP_TO_SURFACE, "oppositeDirection" : true, "depth" : 25 * mm, "endBoundEntityFace" : qUnion([Q7]), "offsetDistance" : 25 * mm});
        }
        {
            var Q0;
            {var subQ0=sQuery(id+"F2.wireOp",EDGE,"E47");Q0=makeQuery(id+"F2.imprint","IMPRINT",FACE,{"disambiguationData":[TD([[makeQuery(id+"F2.imprint","IMPRINT",EDGE,{"derivedFrom":subQ0}),1.0]])]});}
            var Q1;
            {var subQ0=sQuery(id+"F2.wireOp",EDGE,"E45");Q1=makeQuery(id+"F2.imprint","IMPRINT",FACE,{"disambiguationData":[TD([[makeQuery(id+"F2.imprint","IMPRINT",EDGE,{"derivedFrom":subQ0}),1.0]])]});}
            var Q2;
            {var subQ0=sQuery(id+"F2.wireOp",EDGE,"E44.trimOffspring");var subQ1=sQuery(id+"F2.wireOp",EDGE,"E43.trimOffspring");var subQ2=sQuery(id+"F2.wireOp",EDGE,"E39");var subQ3=sQuery(id+"F2.wireOp",EDGE,"E27");var subQ4=sQuery(id+"F2.wireOp",EDGE,"E14.MirrorCS");var subQ5=sQuery(id+"F2.wireOp",EDGE,"E12");var subQ6=sQuery(id+"F2.wireOp",EDGE,"E42.MirrorCS");var subQ7=sQuery(id+"F2.wireOp",EDGE,"E41.MirrorCS");var subQ8=sQuery(id+"F2.wireOp",EDGE,"E32.MirrorCS");var subQ9=sQuery(id+"F2.wireOp",EDGE,"E31.MirrorCS");var subQ10=sQuery(id+"F2.wireOp",EDGE,"E16.MirrorCS");var subQ11=sQuery(id+"F2.wireOp",EDGE,"E15.MirrorCS");Q2=makeQuery(id+"F6.boolean.opBoolean","MERGE",FACE,{"derivedFrom":[makeQuery(id+"F4.boolean.opBoolean","MERGE",FACE,{"derivedFrom":[makeQuery(id+"F1.opExtrude","CAP_FACE",FACE,{"disambiguationData":[OSD([sQuery(id+"F0.wireOp",EDGE,"E0.bottom"),sQuery(id+"F0.wireOp",EDGE,"E0.top"),sQuery(id+"F0.wireOp",EDGE,"E0.left"),sQuery(id+"F0.wireOp",EDGE,"E0.right")])],"isStart":false}),makeQuery(id+"F4.opExtrude","CAP_FACE",FACE,{"disambiguationData":[OSD([subQ5,subQ4,subQ11,subQ10,subQ9,subQ8,subQ7,subQ6])],"isStart":false}),makeQuery(id+"F4.opExtrude","CAP_FACE",FACE,{"disambiguationData":[OSD([subQ5,subQ3,subQ2,subQ1])],"isStart":false}),makeQuery(id+"F4.opExtrude","CAP_FACE",FACE,{"disambiguationData":[OSD([subQ4,subQ3,subQ2,subQ0])],"isStart":false})]}),makeQuery(id+"F6.opExtrude","CAP_FACE",FACE,{"disambiguationData":[OSD([subQ5,subQ4,subQ11,subQ10,subQ9,subQ8,sQuery(id+"F2.wireOp",EDGE,"E33"),sQuery(id+"F2.wireOp",EDGE,"E34"),subQ7,subQ6])],"isStart":false}),makeQuery(id+"F6.opExtrude","CAP_FACE",FACE,{"disambiguationData":[OSD([subQ5,subQ4,subQ3,sQuery(id+"F2.wireOp",EDGE,"E28"),sQuery(id+"F2.wireOp",EDGE,"E29"),sQuery(id+"F2.wireOp",EDGE,"E30"),subQ2,sQuery(id+"F2.wireOp",EDGE,"E40"),subQ1,subQ0])],"isStart":false})]});}
            extrude(context, id + "F8", {"entities" : qUnion([Q0, Q1]), "operationType" : NewBodyOperationType.ADD, "endBound" : BoundingType.UP_TO_SURFACE, "oppositeDirection" : true, "depth" : 25 * mm, "endBoundEntityFace" : qUnion([Q2]), "offsetDistance" : 25 * mm});
        }
        {
            var Q0;
            {var subQ6=sQuery(id+"F2.wireOp",EDGE,"E45");Q0=makeQuery(id+"F2.imprint","IMPRINT",FACE,{"disambiguationData":[TD([[makeQuery(id+"F2.imprint","IMPRINT",EDGE,{"derivedFrom":subQ6}),-1.0]])]});}
            var Q1;
            {var subQ0=sQuery(id+"F2.wireOp",EDGE,"078813e0-c8bc-44f5-a2a2-960b90397534");var subQ1=sQuery(id+"F2.wireOp",EDGE,"E28");var subQ2=makeQuery(id+"F2.imprint","INTERSECT",VERTEX,{"derivedFrom":[subQ1,subQ0]});Q1=makeQuery(id+"F2.imprint","IMPRINT",FACE,{"disambiguationData":[TD([[makeQuery(id+"F2.imprint","IMPRINT",EDGE,{"disambiguationData":[TD([[subQ2,1.0]])],"derivedFrom":subQ1}),-1.0]])]});}
            var Q2;
            {var subQ0=sQuery(id+"F2.wireOp",EDGE,"E10");var subQ1=sQuery(id+"F2.wireOp",EDGE,"E44.trimOffspring");var subQ2=sQuery(id+"F2.wireOp",EDGE,"E39");var subQ3=sQuery(id+"F2.wireOp",EDGE,"E27");var subQ4=sQuery(id+"F2.wireOp",EDGE,"E14.MirrorCS");var subQ5=sQuery(id+"F2.wireOp",EDGE,"E42.MirrorCS");var subQ6=sQuery(id+"F2.wireOp",EDGE,"E41.MirrorCS");var subQ7=sQuery(id+"F2.wireOp",EDGE,"E32.MirrorCS");var subQ8=sQuery(id+"F2.wireOp",EDGE,"E31.MirrorCS");var subQ9=sQuery(id+"F2.wireOp",EDGE,"E16.MirrorCS");var subQ10=sQuery(id+"F2.wireOp",EDGE,"E12");Q2=makeQuery(id+"F8.boolean.opBoolean","MERGE",FACE,{"derivedFrom":[makeQuery(id+"F6.boolean.opBoolean","MERGE",FACE,{"derivedFrom":[makeQuery(id+"F4.boolean.opBoolean","MERGE",FACE,{"derivedFrom":[makeQuery(id+"F1.opExtrude","CAP_FACE",FACE,{"disambiguationData":[OSD([sQuery(id+"F0.wireOp",EDGE,"E0.bottom"),sQuery(id+"F0.wireOp",EDGE,"E0.top"),sQuery(id+"F0.wireOp",EDGE,"E0.left"),sQuery(id+"F0.wireOp",EDGE,"E0.right")])],"isStart":false}),makeQuery(id+"F4.opExtrude","CAP_FACE",FACE,{"disambiguationData":[OSD([subQ10,subQ4,sQuery(id+"F2.wireOp",EDGE,"E15.MirrorCS"),subQ9,subQ8,subQ7,subQ6,subQ5])],"isStart":false}),makeQuery(id+"F4.opExtrude","CAP_FACE",FACE,{"disambiguationData":[OSD([subQ4,subQ3,subQ2,subQ1])],"isStart":false})]}),makeQuery(id+"F6.opExtrude","CAP_FACE",FACE,{"disambiguationData":[OSD([subQ10,subQ4,subQ9,subQ8,subQ7,subQ6,subQ5])],"isStart":false}),makeQuery(id+"F6.opExtrude","CAP_FACE",FACE,{"disambiguationData":[OSD([subQ4,subQ3,sQuery(id+"F2.wireOp",EDGE,"E28"),sQuery(id+"F2.wireOp",EDGE,"E29"),sQuery(id+"F2.wireOp",EDGE,"E30"),subQ2,sQuery(id+"F2.wireOp",EDGE,"E40"),sQuery(id+"F2.wireOp",EDGE,"E43.trimOffspring"),subQ1])],"isStart":false})]}),makeQuery(id+"F8.opExtrude","CAP_FACE",FACE,{"disambiguationData":[OSD([subQ0,sQuery(id+"F2.wireOp",EDGE,"E11"),sQuery(id+"F2.wireOp",EDGE,"E47"),sQuery(id+"F2.wireOp",EDGE,"E48")])],"isStart":false}),makeQuery(id+"F8.opExtrude","CAP_FACE",FACE,{"disambiguationData":[OSD([subQ0,sQuery(id+"F2.wireOp",EDGE,"E45"),sQuery(id+"F2.wireOp",EDGE,"E46"),sQuery(id+"F2.wireOp",EDGE,"3fb50dfe-1aac-44b7-ac28-91fae59e1545")])],"isStart":false})]});}
            extrude(context, id + "F9", {"entities" : qUnion([Q0, Q1]), "operationType" : NewBodyOperationType.REMOVE, "endBound" : BoundingType.UP_TO_SURFACE, "oppositeDirection" : true, "depth" : 25 * mm, "endBoundEntityFace" : qUnion([Q2]), "offsetDistance" : 25 * mm});
        }
        {
            var Q0;
            {var subQ0=sQuery(id+"F2.wireOp",EDGE,"E33");var subQ1=sQuery(id+"F2.wireOp",EDGE,"E12");var subQ2=makeQuery(id+"F2.imprint","INTERSECT",VERTEX,{"derivedFrom":[subQ1,subQ0]});Q0=makeQuery(id+"F2.imprint","IMPRINT",FACE,{"disambiguationData":[TD([[makeQuery(id+"F2.imprint","IMPRINT",EDGE,{"disambiguationData":[TD([[subQ2,1.0]])],"derivedFrom":subQ1}),1.0]])]});}
            var Q1;
            {var subQ0=sQuery(id+"F2.wireOp",EDGE,"E31.MirrorCS");var subQ1=sQuery(id+"F2.wireOp",EDGE,"E12");var subQ2=makeQuery(id+"F2.imprint","INTERSECT",VERTEX,{"derivedFrom":[subQ1,subQ0]});Q1=makeQuery(id+"F2.imprint","IMPRINT",FACE,{"disambiguationData":[TD([[makeQuery(id+"F2.imprint","IMPRINT",EDGE,{"disambiguationData":[TD([[subQ2,1.0]])],"derivedFrom":subQ1}),1.0]])]});}
            var Q2;
            {var subQ0=sQuery(id+"F2.wireOp",EDGE,"E10");var subQ1=sQuery(id+"F2.wireOp",EDGE,"E44.trimOffspring");var subQ2=sQuery(id+"F2.wireOp",EDGE,"E39");var subQ3=sQuery(id+"F2.wireOp",EDGE,"E27");var subQ4=sQuery(id+"F2.wireOp",EDGE,"E14.MirrorCS");var subQ5=sQuery(id+"F2.wireOp",EDGE,"E42.MirrorCS");var subQ6=sQuery(id+"F2.wireOp",EDGE,"E41.MirrorCS");var subQ7=sQuery(id+"F2.wireOp",EDGE,"E32.MirrorCS");var subQ8=sQuery(id+"F2.wireOp",EDGE,"E31.MirrorCS");var subQ9=sQuery(id+"F2.wireOp",EDGE,"E16.MirrorCS");var subQ10=sQuery(id+"F2.wireOp",EDGE,"E12");Q2=makeQuery(id+"F8.boolean.opBoolean","MERGE",FACE,{"derivedFrom":[makeQuery(id+"F6.boolean.opBoolean","MERGE",FACE,{"derivedFrom":[makeQuery(id+"F4.boolean.opBoolean","MERGE",FACE,{"derivedFrom":[makeQuery(id+"F1.opExtrude","CAP_FACE",FACE,{"disambiguationData":[OSD([sQuery(id+"F0.wireOp",EDGE,"E0.bottom"),sQuery(id+"F0.wireOp",EDGE,"E0.top"),sQuery(id+"F0.wireOp",EDGE,"E0.left"),sQuery(id+"F0.wireOp",EDGE,"E0.right")])],"isStart":false}),makeQuery(id+"F4.opExtrude","CAP_FACE",FACE,{"disambiguationData":[OSD([subQ10,subQ4,sQuery(id+"F2.wireOp",EDGE,"E15.MirrorCS"),subQ9,subQ8,subQ7,subQ6,subQ5])],"isStart":false}),makeQuery(id+"F4.opExtrude","CAP_FACE",FACE,{"disambiguationData":[OSD([subQ4,subQ3,subQ2,subQ1])],"isStart":false})]}),makeQuery(id+"F6.opExtrude","CAP_FACE",FACE,{"disambiguationData":[OSD([subQ10,subQ4,subQ9,subQ8,subQ7,subQ6,subQ5])],"isStart":false}),makeQuery(id+"F6.opExtrude","CAP_FACE",FACE,{"disambiguationData":[OSD([subQ4,subQ3,sQuery(id+"F2.wireOp",EDGE,"E28"),sQuery(id+"F2.wireOp",EDGE,"E29"),sQuery(id+"F2.wireOp",EDGE,"E30"),subQ2,sQuery(id+"F2.wireOp",EDGE,"E40"),sQuery(id+"F2.wireOp",EDGE,"E43.trimOffspring"),subQ1])],"isStart":false})]}),makeQuery(id+"F8.opExtrude","CAP_FACE",FACE,{"disambiguationData":[OSD([subQ0,sQuery(id+"F2.wireOp",EDGE,"E11"),sQuery(id+"F2.wireOp",EDGE,"E47"),sQuery(id+"F2.wireOp",EDGE,"E48")])],"isStart":false}),makeQuery(id+"F8.opExtrude","CAP_FACE",FACE,{"disambiguationData":[OSD([subQ0,sQuery(id+"F2.wireOp",EDGE,"E45"),sQuery(id+"F2.wireOp",EDGE,"E46"),sQuery(id+"F2.wireOp",EDGE,"3fb50dfe-1aac-44b7-ac28-91fae59e1545")])],"isStart":false})]});}
            extrude(context, id + "F10", {"entities" : qUnion([Q0, Q1]), "operationType" : NewBodyOperationType.ADD, "endBound" : BoundingType.UP_TO_SURFACE, "oppositeDirection" : true, "depth" : 25 * mm, "endBoundEntityFace" : qUnion([Q2]), "offsetDistance" : 25 * mm});
        }
        {
            var Q0;
            {var subQ0=sQuery(id+"F2.wireOp",EDGE,"E53");Q0=makeQuery(id+"F2.imprint","IMPRINT",FACE,{"disambiguationData":[TD([[makeQuery(id+"F2.imprint","IMPRINT",EDGE,{"derivedFrom":subQ0}),-1.0]])]});}
            var Q1;
            {var subQ0=sQuery(id+"F2.wireOp",EDGE,"E55");Q1=makeQuery(id+"F2.imprint","IMPRINT",FACE,{"disambiguationData":[TD([[makeQuery(id+"F2.imprint","IMPRINT",EDGE,{"derivedFrom":subQ0}),1.0]])]});}
            var Q2;
            {var subQ0=sQuery(id+"F2.wireOp",EDGE,"E15.MirrorCS");var subQ1=sQuery(id+"F2.wireOp",EDGE,"E12");var subQ2=sQuery(id+"F2.wireOp",EDGE,"E32.MirrorCS");var subQ3=sQuery(id+"F2.wireOp",EDGE,"E31.MirrorCS");var subQ4=sQuery(id+"F2.wireOp",EDGE,"E43.trimOffspring");var subQ5=sQuery(id+"F2.wireOp",EDGE,"E40");var subQ6=sQuery(id+"F2.wireOp",EDGE,"E39");var subQ7=sQuery(id+"F2.wireOp",EDGE,"E14.MirrorCS");var subQ8=sQuery(id+"F0.wireOp",EDGE,"E0.right");var subQ9=sQuery(id+"F0.wireOp",EDGE,"E0.left");var subQ10=sQuery(id+"F0.wireOp",EDGE,"E0.top");var subQ11=sQuery(id+"F0.wireOp",EDGE,"E0.bottom");var subQ12=sQuery(id+"F2.wireOp",EDGE,"E44.trimOffspring");var subQ13=sQuery(id+"F2.wireOp",EDGE,"E27");var subQ14=sQuery(id+"F2.wireOp",EDGE,"E42.MirrorCS");var subQ15=sQuery(id+"F2.wireOp",EDGE,"E41.MirrorCS");var subQ16=sQuery(id+"F2.wireOp",EDGE,"E16.MirrorCS");Q2=makeQuery(id+"F10.boolean.opBoolean","MERGE",FACE,{"derivedFrom":[makeQuery(id+"F8.boolean.opBoolean","MERGE",FACE,{"derivedFrom":[makeQuery(id+"F6.boolean.opBoolean","MERGE",FACE,{"derivedFrom":[makeQuery(id+"F4.boolean.opBoolean","MERGE",FACE,{"derivedFrom":[makeQuery(id+"F1.opExtrude","CAP_FACE",FACE,{"disambiguationData":[OSD([subQ11,subQ10,subQ9,subQ8])],"isStart":false}),makeQuery(id+"F4.opExtrude","CAP_FACE",FACE,{"disambiguationData":[OSD([subQ1,subQ7,subQ0,subQ16,subQ3,subQ2,subQ15,subQ14])],"isStart":false}),makeQuery(id+"F4.opExtrude","CAP_FACE",FACE,{"disambiguationData":[OSD([subQ7,subQ13,subQ6,subQ12])],"isStart":false})]}),makeQuery(id+"F6.opExtrude","CAP_FACE",FACE,{"disambiguationData":[OSD([subQ1,subQ7,subQ16,subQ3,subQ2,subQ15,subQ14])],"isStart":false}),makeQuery(id+"F6.opExtrude","CAP_FACE",FACE,{"disambiguationData":[OSD([subQ7,subQ13,sQuery(id+"F2.wireOp",EDGE,"E28"),sQuery(id+"F2.wireOp",EDGE,"E29"),sQuery(id+"F2.wireOp",EDGE,"E30"),subQ6,subQ5,subQ4,subQ12])],"isStart":false})]}),makeQuery(id+"F8.opExtrude","CAP_FACE",FACE,{"disambiguationData":[OSD([subQ11,subQ10,subQ9,subQ8,sQuery(id+"F2.wireOp",EDGE,"E1.bottom"),sQuery(id+"F2.wireOp",EDGE,"E1.left"),sQuery(id+"F2.wireOp",EDGE,"E1.right"),sQuery(id+"F2.wireOp",EDGE,"E3"),sQuery(id+"F2.wireOp",EDGE,"E4"),sQuery(id+"F2.wireOp",EDGE,"E5"),sQuery(id+"F2.wireOp",EDGE,"E7"),sQuery(id+"F2.wireOp",EDGE,"E8"),sQuery(id+"F2.wireOp",EDGE,"E9"),sQuery(id+"F2.wireOp",EDGE,"E10"),sQuery(id+"F2.wireOp",EDGE,"E11"),subQ1,sQuery(id+"F2.wireOp",EDGE,"E13.MirrorCS"),subQ7,sQuery(id+"F2.wireOp",EDGE,"E17.trimOffspring"),sQuery(id+"F2.wireOp",EDGE,"E18.trimOffspring"),sQuery(id+"F2.wireOp",EDGE,"E19.trimOffspring"),sQuery(id+"F2.wireOp",EDGE,"E20.trimOffspring"),sQuery(id+"F2.wireOp",EDGE,"E21.trimOffspring"),sQuery(id+"F2.wireOp",EDGE,"E22.trimOffspring"),sQuery(id+"F2.wireOp",EDGE,"E23.trimOffspring"),sQuery(id+"F2.wireOp",EDGE,"E24.trimOffspring"),sQuery(id+"F2.wireOp",EDGE,"E25.trimOffspring"),sQuery(id+"F2.wireOp",EDGE,"E37"),sQuery(id+"F2.wireOp",EDGE,"E38"),subQ6,subQ5,subQ4,sQuery(id+"F2.wireOp",EDGE,"E45"),sQuery(id+"F2.wireOp",EDGE,"E46"),sQuery(id+"F2.wireOp",EDGE,"E47"),sQuery(id+"F2.wireOp",EDGE,"E48"),sQuery(id+"F2.wireOp",EDGE,"E49"),sQuery(id+"F2.wireOp",EDGE,"E50"),sQuery(id+"F2.wireOp",EDGE,"E51"),sQuery(id+"F2.wireOp",EDGE,"E52")])],"isStart":false})]}),makeQuery(id+"F10.opExtrude","CAP_FACE",FACE,{"disambiguationData":[OSD([subQ1,subQ0,subQ3,subQ2])],"isStart":false}),makeQuery(id+"F10.opExtrude","CAP_FACE",FACE,{"disambiguationData":[OSD([subQ1,subQ0,sQuery(id+"F2.wireOp",EDGE,"E33"),sQuery(id+"F2.wireOp",EDGE,"E34")])],"isStart":false})]});}
            extrude(context, id + "F11", {"entities" : qUnion([Q0, Q1]), "operationType" : NewBodyOperationType.ADD, "endBound" : BoundingType.UP_TO_SURFACE, "oppositeDirection" : true, "depth" : 25 * mm, "endBoundEntityFace" : qUnion([Q2]), "offsetDistance" : 25 * mm});
        }
        {
            var Q0;
            Q0=makeQuery(id+"F1.opExtrude","SWEPT_FACE",FACE,{"disambiguationData":[OSD([sQuery(id+"F0.wireOp",EDGE,"E0.left")])]});
            var sketch = newSketch(context, id + "F12", { "sketchPlane" : qUnion([Q0])});
            skLineSegment(sketch, "E57", {"start": v(150, -500) * mm, "end": v(150, -350) * mm});
            skLineSegment(sketch, "E58", {"start": v(150, -350) * mm, "end": v(170, -350) * mm});
            skSolve(sketch);
        }
        {
            var Q0;
            {var subQ0=sQuery(id+"F12.wireOp",EDGE,"E57");Q0=makeQuery(id+"F12.imprint","IMPRINT",FACE,{"disambiguationData":[TD([[makeQuery(id+"F12.imprint","IMPRINT",EDGE,{"derivedFrom":subQ0}),-1.0]])]});}
            var Q1;
            Q1=makeQuery(id+"F1.opExtrude","SWEPT_FACE",FACE,{"disambiguationData":[OSD([sQuery(id+"F0.wireOp",EDGE,"E0.right")])]});
            extrude(context, id + "F13", {"entities" : qUnion([Q0]), "operationType" : NewBodyOperationType.REMOVE, "endBound" : BoundingType.UP_TO_SURFACE, "oppositeDirection" : true, "depth" : 25 * mm, "endBoundEntityFace" : qUnion([Q1]), "offsetDistance" : 25 * mm});
        }
        {
            var Q0;
            Q0=makeQuery(id+"F1.opExtrude","SWEPT_FACE",FACE,{"disambiguationData":[OSD([sQuery(id+"F0.wireOp",EDGE,"E0.left")])]});
            var sketch = newSketch(context, id + "F14", { "sketchPlane" : qUnion([Q0])});
            skLineSegment(sketch, "E59", {"start": v(150, 500) * mm, "end": v(150, 475) * mm});
            skLineSegment(sketch, "E60", {"start": v(150, 475) * mm, "end": v(170, 475) * mm});
            skSolve(sketch);
        }
        {
            var Q0;
            {var subQ0=sQuery(id+"F14.wireOp",EDGE,"E59");Q0=makeQuery(id+"F14.imprint","IMPRINT",FACE,{"disambiguationData":[TD([[makeQuery(id+"F14.imprint","IMPRINT",EDGE,{"derivedFrom":subQ0}),1.0]])]});}
            var Q1;
            Q1=makeQuery(id+"F1.opExtrude","SWEPT_FACE",FACE,{"disambiguationData":[OSD([sQuery(id+"F0.wireOp",EDGE,"E0.right")])]});
            extrude(context, id + "F15", {"entities" : qUnion([Q0]), "operationType" : NewBodyOperationType.REMOVE, "endBound" : BoundingType.UP_TO_SURFACE, "oppositeDirection" : true, "depth" : 25 * mm, "endBoundEntityFace" : qUnion([Q1]), "offsetDistance" : 25 * mm});
        }
        {
            var Q0;
            {var subQ12=sQuery(id+"F0.wireOp",EDGE,"E0.right");Q0=makeQuery(id+"F13.boolean.opBoolean","COPY",FACE,{"disambiguationData":[TD([makeQuery(id+"F1.opExtrude","SWEPT_FACE",FACE,{"disambiguationData":[OSD([subQ12])]})])],"derivedFrom":makeQuery(id+"F13.opExtrude","SWEPT_FACE",FACE,{"disambiguationData":[OSD([sQuery(id+"F12.wireOp",EDGE,"E58")])]})});}
            var sketch = newSketch(context, id + "F16", { "sketchPlane" : qUnion([Q0])});
            skArc(sketch, "E61", {"start": v(-742.5, -170) * mm, "mid": v(-747.5, -165) * mm, "end": v(-752.5, -170) * mm});
            skSolve(sketch);
        }
        {
            var Q0;
            {var subQ0=sQuery(id+"F16.wireOp",EDGE,"E61");Q0=makeQuery(id+"F16.imprint","IMPRINT",FACE,{"disambiguationData":[TD([[makeQuery(id+"F16.imprint","IMPRINT",EDGE,{"derivedFrom":subQ0}),1.0]])]});}
            var Q1;
            {var subQ13=sQuery(id+"F0.wireOp",EDGE,"E0.right");Q1=makeQuery(id+"F15.boolean.opBoolean","COPY",FACE,{"disambiguationData":[TD([makeQuery(id+"F1.opExtrude","SWEPT_FACE",FACE,{"disambiguationData":[OSD([subQ13])]})])],"derivedFrom":makeQuery(id+"F15.opExtrude","SWEPT_FACE",FACE,{"disambiguationData":[OSD([sQuery(id+"F14.wireOp",EDGE,"E60")])]})});}
            extrude(context, id + "F17", {"entities" : qUnion([Q0]), "operationType" : NewBodyOperationType.REMOVE, "endBound" : BoundingType.UP_TO_SURFACE, "oppositeDirection" : true, "depth" : 25 * mm, "endBoundEntityFace" : qUnion([Q1]), "offsetDistance" : 25 * mm});
        }
        {
            var Q0;
            {var subQ11=sQuery(id+"F0.wireOp",EDGE,"E0.left");Q0=makeQuery(id+"F13.boolean.opBoolean","COPY",FACE,{"disambiguationData":[TD([makeQuery(id+"F1.opExtrude","SWEPT_FACE",FACE,{"disambiguationData":[OSD([subQ11])]})])],"derivedFrom":makeQuery(id+"F13.opExtrude","SWEPT_FACE",FACE,{"disambiguationData":[OSD([sQuery(id+"F12.wireOp",EDGE,"E58")])]})});}
            var sketch = newSketch(context, id + "F18", { "sketchPlane" : qUnion([Q0])});
            skArc(sketch, "E62", {"start": v(752.5, -170) * mm, "mid": v(747.5, -165) * mm, "end": v(742.5, -170) * mm});
            skSolve(sketch);
        }
        {
            var Q0;
            {var subQ0=sQuery(id+"F18.wireOp",EDGE,"E62");Q0=makeQuery(id+"F18.imprint","IMPRINT",FACE,{"disambiguationData":[TD([[makeQuery(id+"F18.imprint","IMPRINT",EDGE,{"derivedFrom":subQ0}),1.0]])]});}
            var Q1;
            {var subQ12=sQuery(id+"F0.wireOp",EDGE,"E0.left");Q1=makeQuery(id+"F15.boolean.opBoolean","COPY",FACE,{"disambiguationData":[TD([makeQuery(id+"F1.opExtrude","SWEPT_FACE",FACE,{"disambiguationData":[OSD([subQ12])]})])],"derivedFrom":makeQuery(id+"F15.opExtrude","SWEPT_FACE",FACE,{"disambiguationData":[OSD([sQuery(id+"F14.wireOp",EDGE,"E60")])]})});}
            extrude(context, id + "F19", {"entities" : qUnion([Q0]), "operationType" : NewBodyOperationType.REMOVE, "endBound" : BoundingType.UP_TO_SURFACE, "oppositeDirection" : true, "depth" : 25 * mm, "endBoundEntityFace" : qUnion([Q1]), "offsetDistance" : 25 * mm});
        }
        {
            var Q0;
            Q0=makeQuery(id+"F3.boolean.opBoolean","COPY",FACE,{"derivedFrom":makeQuery(id+"F3.opExtrude","SWEPT_FACE",FACE,{"disambiguationData":[OSD([sQuery(id+"F2.wireOp",EDGE,"E7")])]})});
            var sketch = newSketch(context, id + "F20", { "sketchPlane" : qUnion([Q0])});
            skArc(sketch, "E63", {"start": v(5, -170) * mm, "mid": v(0, -165) * mm, "end": v(-5, -170) * mm});
            skSolve(sketch);
        }
        {
            var Q0;
            {var subQ0=sQuery(id+"F20.wireOp",EDGE,"E63");Q0=makeQuery(id+"F20.imprint","IMPRINT",FACE,{"disambiguationData":[TD([[makeQuery(id+"F20.imprint","IMPRINT",EDGE,{"derivedFrom":subQ0}),1.0]])]});}
            var Q1;
            Q1=makeQuery(id+"F3.boolean.opBoolean","COPY",FACE,{"derivedFrom":makeQuery(id+"F3.opExtrude","SWEPT_FACE",FACE,{"disambiguationData":[OSD([sQuery(id+"F2.wireOp",EDGE,"E13.MirrorCS")])]})});
            extrude(context, id + "F21", {"entities" : qUnion([Q0]), "operationType" : NewBodyOperationType.REMOVE, "endBound" : BoundingType.UP_TO_SURFACE, "oppositeDirection" : true, "depth" : 25 * mm, "endBoundEntityFace" : qUnion([Q1]), "offsetDistance" : 25 * mm});
        }
        {
            var Q0;
            {var subQ0=sQuery(id+"F2.wireOp",EDGE,"E40");var subQ2=sQuery(id+"F2.wireOp",EDGE,"E22.trimOffspring");var subQ3=sQuery(id+"F2.wireOp",EDGE,"E1.right");var subQ5=sQuery(id+"F2.wireOp",EDGE,"E28");var subQ7=sQuery(id+"F2.wireOp",EDGE,"E44.trimOffspring");var subQ9=sQuery(id+"F2.wireOp",EDGE,"E51");var subQ10=sQuery(id+"F2.wireOp",EDGE,"E43.trimOffspring");var subQ12=sQuery(id+"F2.wireOp",EDGE,"E27");var subQ14=sQuery(id+"F2.wireOp",EDGE,"E38");var subQ15=sQuery(id+"F2.wireOp",EDGE,"E24.trimOffspring");var subQ16=sQuery(id+"F2.wireOp",EDGE,"E17.trimOffspring");var subQ18=sQuery(id+"F2.wireOp",EDGE,"E10");var subQ20=sQuery(id+"F2.wireOp",EDGE,"E14.MirrorCS");var subQ23=sQuery(id+"F2.wireOp",EDGE,"E30");var subQ25=sQuery(id+"F2.wireOp",EDGE,"E29");var subQ28=sQuery(id+"F2.wireOp",EDGE,"E39");var subQ32=sQuery(id+"F2.wireOp",EDGE,"E52");var subQ34=sQuery(id+"F2.wireOp",EDGE,"E7");var subQ37=sQuery(id+"F2.wireOp",EDGE,"E50");var subQ38=sQuery(id+"F2.wireOp",EDGE,"E45");var subQ40=sQuery(id+"F2.wireOp",EDGE,"E5");var subQ41=makeQuery(id+"F3.boolean.opBoolean","COPY",FACE,{"derivedFrom":makeQuery(id+"F3.opExtrude","SWEPT_FACE",FACE,{"disambiguationData":[OSD([subQ40])]})});var subQ42=sQuery(id+"F2.wireOp",EDGE,"E8");var subQ44=sQuery(id+"F2.wireOp",EDGE,"E53");var subQ47=sQuery(id+"F2.wireOp",EDGE,"E13.MirrorCS");var subQ49=sQuery(id+"F2.wireOp",EDGE,"E9");var subQ51=sQuery(id+"F2.wireOp",EDGE,"E54");var subQ53=sQuery(id+"F2.wireOp",EDGE,"E23.trimOffspring");var subQ57=sQuery(id+"F2.wireOp",EDGE,"E42.MirrorCS");var subQ58=sQuery(id+"F2.wireOp",EDGE,"E41.MirrorCS");var subQ59=sQuery(id+"F2.wireOp",EDGE,"E32.MirrorCS");var subQ60=sQuery(id+"F2.wireOp",EDGE,"E31.MirrorCS");var subQ61=sQuery(id+"F2.wireOp",EDGE,"E16.MirrorCS");var subQ62=sQuery(id+"F2.wireOp",EDGE,"E12");var subQ63=makeQuery(id+"F6.opExtrude","CAP_FACE",FACE,{"disambiguationData":[OSD([subQ62,subQ20,subQ61,subQ60,subQ59,subQ58,subQ57])],"isStart":false});var subQ64=makeQuery(id+"F4.opExtrude","CAP_FACE",FACE,{"disambiguationData":[OSD([subQ20,subQ12,subQ28,subQ7])],"isStart":false});var subQ65=sQuery(id+"F2.wireOp",EDGE,"E15.MirrorCS");var subQ66=makeQuery(id+"F4.opExtrude","CAP_FACE",FACE,{"disambiguationData":[OSD([subQ62,subQ20,subQ65,subQ61,subQ60,subQ59,subQ58,subQ57])],"isStart":false});var subQ67=sQuery(id+"F0.wireOp",EDGE,"E0.right");var subQ68=sQuery(id+"F0.wireOp",EDGE,"E0.left");var subQ69=sQuery(id+"F0.wireOp",EDGE,"E0.top");var subQ70=sQuery(id+"F0.wireOp",EDGE,"E0.bottom");var subQ71=makeQuery(id+"F1.opExtrude","CAP_FACE",FACE,{"disambiguationData":[OSD([subQ70,subQ69,subQ68,subQ67])],"isStart":false});var subQ72=makeQuery(id+"F10.opExtrude","CAP_FACE",FACE,{"disambiguationData":[OSD([subQ62,subQ65,subQ60,subQ59])],"isStart":false});var subQ73=sQuery(id+"F2.wireOp",EDGE,"E4");var subQ75=makeQuery(id+"F1.opExtrude","SWEPT_FACE",FACE,{"disambiguationData":[OSD([subQ68])]});var subQ76=sQuery(id+"F2.wireOp",EDGE,"E49");var subQ77=sQuery(id+"F2.wireOp",EDGE,"E48");var subQ78=sQuery(id+"F2.wireOp",EDGE,"E47");var subQ79=sQuery(id+"F2.wireOp",EDGE,"E46");var subQ80=sQuery(id+"F2.wireOp",EDGE,"E37");var subQ81=sQuery(id+"F2.wireOp",EDGE,"E25.trimOffspring");var subQ82=sQuery(id+"F2.wireOp",EDGE,"E21.trimOffspring");var subQ83=sQuery(id+"F2.wireOp",EDGE,"E20.trimOffspring");var subQ84=sQuery(id+"F2.wireOp",EDGE,"E19.trimOffspring");var subQ85=sQuery(id+"F2.wireOp",EDGE,"E18.trimOffspring");var subQ86=sQuery(id+"F2.wireOp",EDGE,"E11");var subQ87=sQuery(id+"F2.wireOp",EDGE,"E3");var subQ88=sQuery(id+"F2.wireOp",EDGE,"E1.left");var subQ89=makeQuery(id+"F8.opExtrude","CAP_FACE",FACE,{"disambiguationData":[OSD([subQ70,subQ69,subQ68,subQ67,sQuery(id+"F2.wireOp",EDGE,"E1.bottom"),subQ88,subQ3,subQ87,subQ73,subQ40,subQ34,subQ42,subQ49,subQ18,subQ86,subQ62,subQ47,subQ20,subQ16,subQ85,subQ84,subQ83,subQ82,subQ2,subQ53,subQ15,subQ81,subQ80,subQ14,subQ28,subQ0,subQ10,subQ38,subQ79,subQ78,subQ77,subQ76,subQ37,subQ9,subQ32])],"isStart":false});var subQ90=makeQuery(id+"F6.opExtrude","CAP_FACE",FACE,{"disambiguationData":[OSD([subQ20,subQ12,subQ5,subQ25,subQ23,subQ28,subQ0,subQ10,subQ7])],"isStart":false});var subQ91=sQuery(id+"F2.wireOp",EDGE,"E34");var subQ92=sQuery(id+"F2.wireOp",EDGE,"E33");var subQ93=makeQuery(id+"F10.opExtrude","CAP_FACE",FACE,{"disambiguationData":[OSD([subQ62,subQ65,subQ92,subQ91])],"isStart":false});var subQ94=sQuery(id+"F2.wireOp",EDGE,"E56");var subQ95=sQuery(id+"F2.wireOp",EDGE,"E55");var subQ96=makeQuery(id+"F11.opExtrude","CAP_FACE",FACE,{"disambiguationData":[OSD([subQ18,subQ86,subQ95,subQ94])],"isStart":false});var subQ97=makeQuery(id+"F11.opExtrude","CAP_FACE",FACE,{"disambiguationData":[OSD([subQ18,subQ32,subQ44,subQ51])],"isStart":false});var subQ125=makeQuery(id+"F3.boolean.opBoolean","COPY",FACE,{"derivedFrom":makeQuery(id+"F3.opExtrude","SWEPT_FACE",FACE,{"disambiguationData":[OSD([subQ88])]})});Q0=makeQuery(id+"F21.boolean.opBoolean","SPLIT",FACE,{"disambiguationData":[TD([subQ41])],"derivedFrom":makeQuery(id+"F19.boolean.opBoolean","SPLIT",FACE,{"disambiguationData":[TD([subQ125])],"derivedFrom":makeQuery(id+"F17.boolean.opBoolean","SPLIT",FACE,{"disambiguationData":[TD([subQ75])],"derivedFrom":makeQuery(id+"F11.boolean.opBoolean","MERGE",FACE,{"derivedFrom":[makeQuery(id+"F10.boolean.opBoolean","MERGE",FACE,{"derivedFrom":[makeQuery(id+"F8.boolean.opBoolean","MERGE",FACE,{"derivedFrom":[makeQuery(id+"F6.boolean.opBoolean","MERGE",FACE,{"derivedFrom":[makeQuery(id+"F4.boolean.opBoolean","MERGE",FACE,{"derivedFrom":[subQ71,subQ66,subQ64]}),subQ63,subQ90]}),subQ89]}),subQ72,subQ93]}),subQ96,subQ97]})})})});}
            var sketch = newSketch(context, id + "F22", { "sketchPlane" : qUnion([Q0])});
            skLineSegment(sketch, "E64", {"start": v(-747.5, 307.5) * mm, "end": v(0, 307.5) * mm});
            skLineSegment(sketch, "E65", {"start": v(0, 307.5) * mm, "end": v(747.5, 307.5) * mm});
            skSolve(sketch);
        }
        {
            var Q0;
            Q0=qCreatedBy(makeId("Right.planeOp"),FACE);
            var sketch = newSketch(context, id + "F23", { "sketchPlane" : qUnion([Q0])});
            skCircle(sketch, "E66", {"center": v(170, 307.5) * mm, "radius": 5 * mm});
            skSolve(sketch);
        }
        {
            var Q0;
            Q0=makeQuery(id+"F23.imprint","IMPRINT",FACE,{"disambiguationData":[TD([[makeQuery(id+"F23.imprint","IMPRINT",EDGE,{"derivedFrom":sQuery(id+"F23.wireOp",EDGE,"E66")}),1.0]])]});
            var Q1;
            Q1=sQuery(id+"F22.wireOp",EDGE,"E64");
            var Q2;
            Q2=sQuery(id+"F22.wireOp",EDGE,"E65");
            sweep(context, id + "F24", {"operationType" : NewBodyOperationType.REMOVE, "profiles" : qUnion([Q0]), "path" : qUnion([Q1, Q2])});
        }
    });
